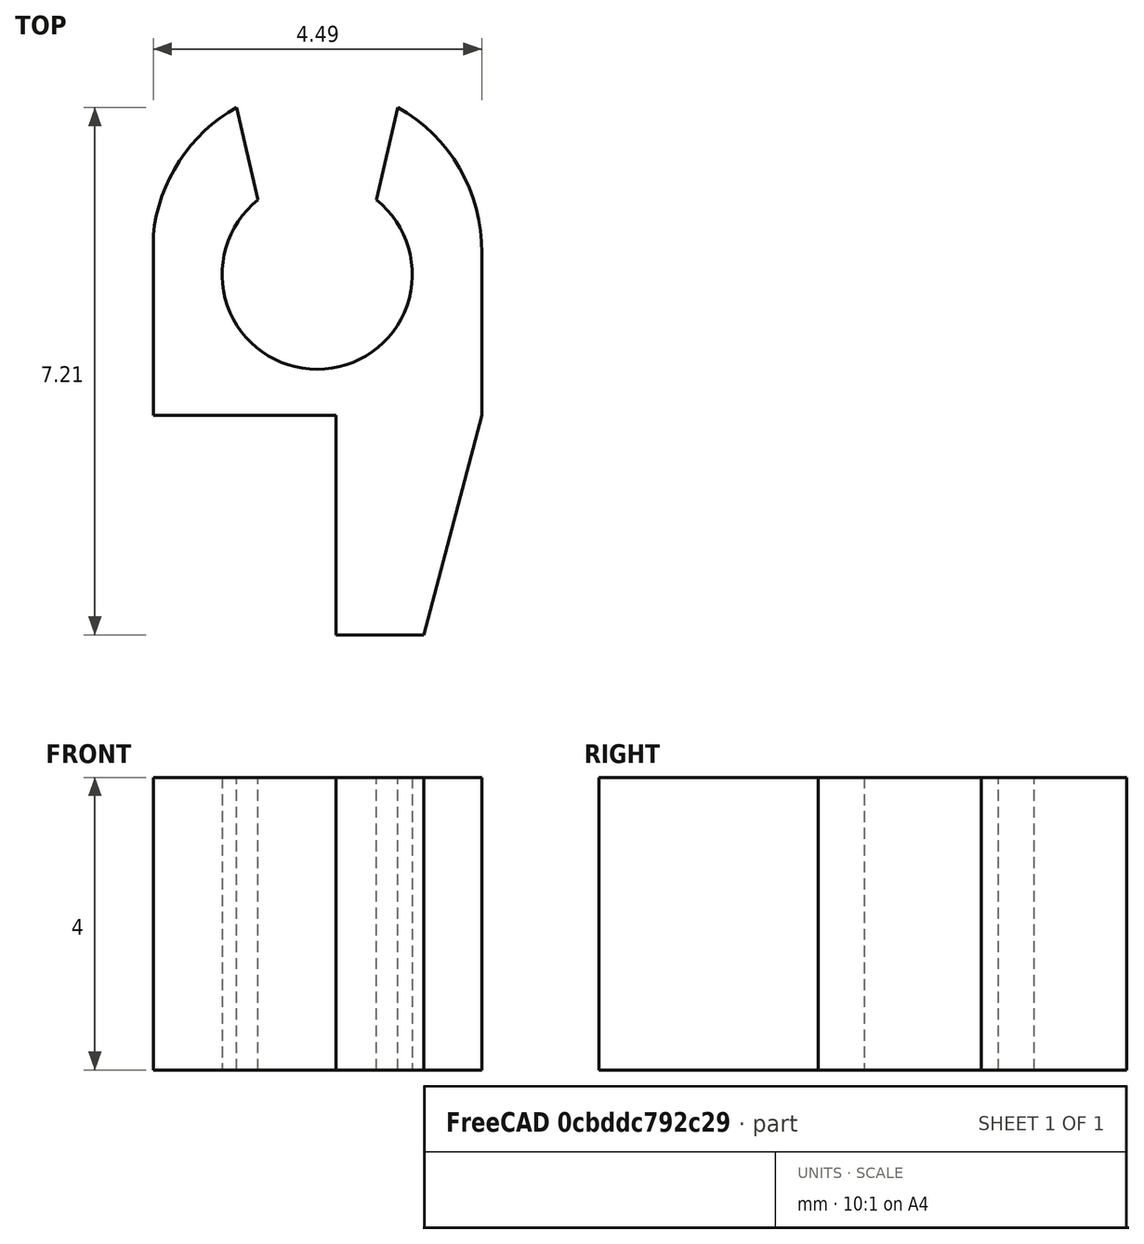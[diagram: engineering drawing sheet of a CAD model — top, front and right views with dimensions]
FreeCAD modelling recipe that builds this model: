
FCSTD DOCUMENT  (FreeCAD 0.20R29603 (Git))
Label: drzac_kabla_v2
License: All rights reserved
LicenseURL: http://en.wikipedia.org/wiki/All_rights_reserved
objects: Sketcher::SketchObject×1, PartDesign::Pad×1, PartDesign::Body×1
note: 4 computed .brp shape members not serialized (recipe doc carries the construction recipe); baked Part::Feature solids carry a one-line shape summary decoded from their .brp

FEATURE [Sketcher::SketchObject] Sketch
  FullyConstrained = false
  MapMode = 5
  Support = -> [XY_Plane]
  sketch-geometry (12):
    g0: ArcOfCircle CenterX=0 CenterY=2.25 CenterZ=0 NormalX=0 NormalY=0 NormalZ=1 AngleXU=0 Radius=2.25 StartAngle=6.27206 EndAngle=7.34317
    g1: LineSegment StartX=-2.24 StartY=2.4619 StartZ=0 EndX=-2.24 EndY=0 EndZ=0
    g2: LineSegment StartX=-2.24 StartY=0 StartZ=0 EndX=0.26 EndY=0 EndZ=0
    g3: LineSegment StartX=-1.1 StartY=4.21278 StartZ=0 EndX=1.1 EndY=4.21278 EndZ=0
    g4: ArcOfCircle CenterX=0 CenterY=2.25 CenterZ=0 NormalX=0 NormalY=0 NormalZ=1 AngleXU=0 Radius=2.25 StartAngle=2.08161 EndAngle=3.04728
    g5: LineSegment StartX=0.26 StartY=0 StartZ=0 EndX=0.26 EndY=-3 EndZ=0
    g6: LineSegment StartX=0.26 StartY=-3 StartZ=0 EndX=1.46 EndY=-3 EndZ=0
    g7: LineSegment StartX=2.24986 StartY=2.22497 StartZ=0 EndX=2.24986 EndY=0 EndZ=0
    g8: ArcOfCircle CenterX=0 CenterY=1.93 CenterZ=0 NormalX=0 NormalY=0 NormalZ=1 AngleXU=0 Radius=1.3 StartAngle=2.2406 EndAngle=7.18418
    g9: LineSegment StartX=-1.1 StartY=4.21278 StartZ=0 EndX=-0.807079 EndY=2.94913 EndZ=0
    g10: LineSegment StartX=1.1 StartY=4.21278 StartZ=0 EndX=0.807079 EndY=2.94913 EndZ=0
    g11: LineSegment StartX=1.46 StartY=-3 StartZ=0 EndX=2.24986 EndY=0 EndZ=0
  constraints (37):
    c: Diameter(g0) = 4.5
    c: PointOnObject(g-1,g0)
    c: Vertical(g1)
    c: PointOnObject(g1,g-1)
    c: Coincident(g2,g1)
    c: PointOnObject(g2,g-1)
    c: DistanceX(g2,g2) = 2.5
    c: Coincident(g4,g1) = -1.5708
    c: PointOnObject(g3,g0)
    c: PointOnObject(g3,g0)
    c: Horizontal(g3)
    c: DistanceX(g3,g3) = 2.2
    c: Equal(g0,g4)
    c: PointOnObject(g0,g3)
    c: PointOnObject(g4,g3)
    c: Coincident(g0,g4)
    c: Coincident(g5,g2)
    c: Vertical(g5)
    c: Coincident(g6,g5)
    c: Horizontal(g6)
    c: DistanceY(g5,g5) = 3
    c: Coincident(g7,g0)
    c: Vertical(g7)
    c: PointOnObject(g8,g-2)
    c: Diameter(g8) = 2.6
    c: Coincident(g9,g4)
    c: Coincident(g10,g0)
    c: Equal(g10,g9)
    c: PointOnObject(g0,g-2)
    c: DistanceY(g-1,g8) = 1.93
    c: Coincident(g8,g10)
    c: Coincident(g8,g9)
    c: DistanceX(g5,g11) = 1.2
    c: PointOnObject(g11,g-1)
    c: Coincident(g6,g11)
    c: Coincident(g7,g11)
    c: DistanceX(g1,g-1) = 2.24
FEATURE [PartDesign::Pad] Pad
  Direction = (0,0,1)
  Length = 4
  Length2 = 10
  Profile = -> Sketch
  ReferenceAxis = -> Sketch [N_Axis]
  Type = 0
FEATURE [PartDesign::Body] Body
  Group = -> [Sketch,Pad]
  Origin = -> Origin
  Tip = -> Pad
